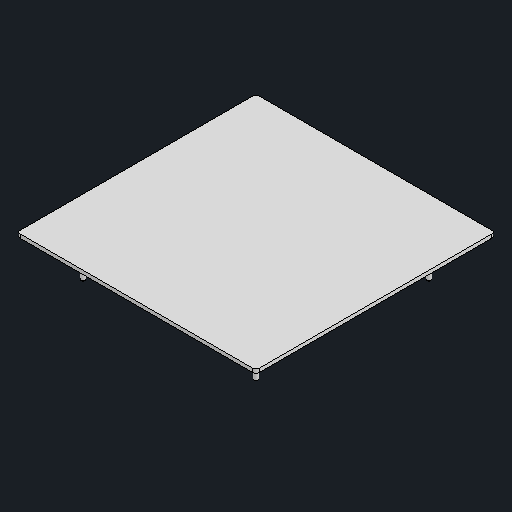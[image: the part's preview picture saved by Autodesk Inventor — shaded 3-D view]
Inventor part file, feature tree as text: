
AUTODESK INVENTOR PART (.ipt)
format: ipt  version: 2024.2 (Build 282272000, 272)  size: 2,296,832 bytes
history: native  units: mm
features: other x10, mirror x6, chamfer x1, sweep x1
ambient origin geometry x8: Origin, YZ Plane, XZ Plane, XY Plane, X Axis, Y Axis, Z Axis, Center Point
bodies: Body1 (feature_tree), Body2 (feature_tree), Body3 (feature_tree), Body4 (feature_tree), Body5 (feature_tree), Body6 (feature_tree), Body7 (feature_tree), Body8 (feature_tree), Body9 (feature_tree)
feature tree (18):
  other  "솔리드1"
  other  "솔리드2"
  other  "솔리드3"
  other  "솔리드4"
  other  "솔리드5"
  other  "솔리드6"
  other  "솔리드7"
  other  "솔리드8"
  other  "솔리드9"
  chamfer  "Chamfer1"  [1 undecoded]
  other  "Boss-Extrude3"
  sweep  "Sweep1"
  mirror  "Mirror1[1]"
  mirror  "Mirror2[1]"
  mirror  "Mirror2[2]"
  mirror  "Mirror1[2]"
  mirror  "Mirror2[3]"
  mirror  "Mirror2[4]"
note: 1 required parameter value undecoded (feature->parameter linkage not recoverable at this tier; creation-order binding heuristic only, values carry confidence <= 0.55)
